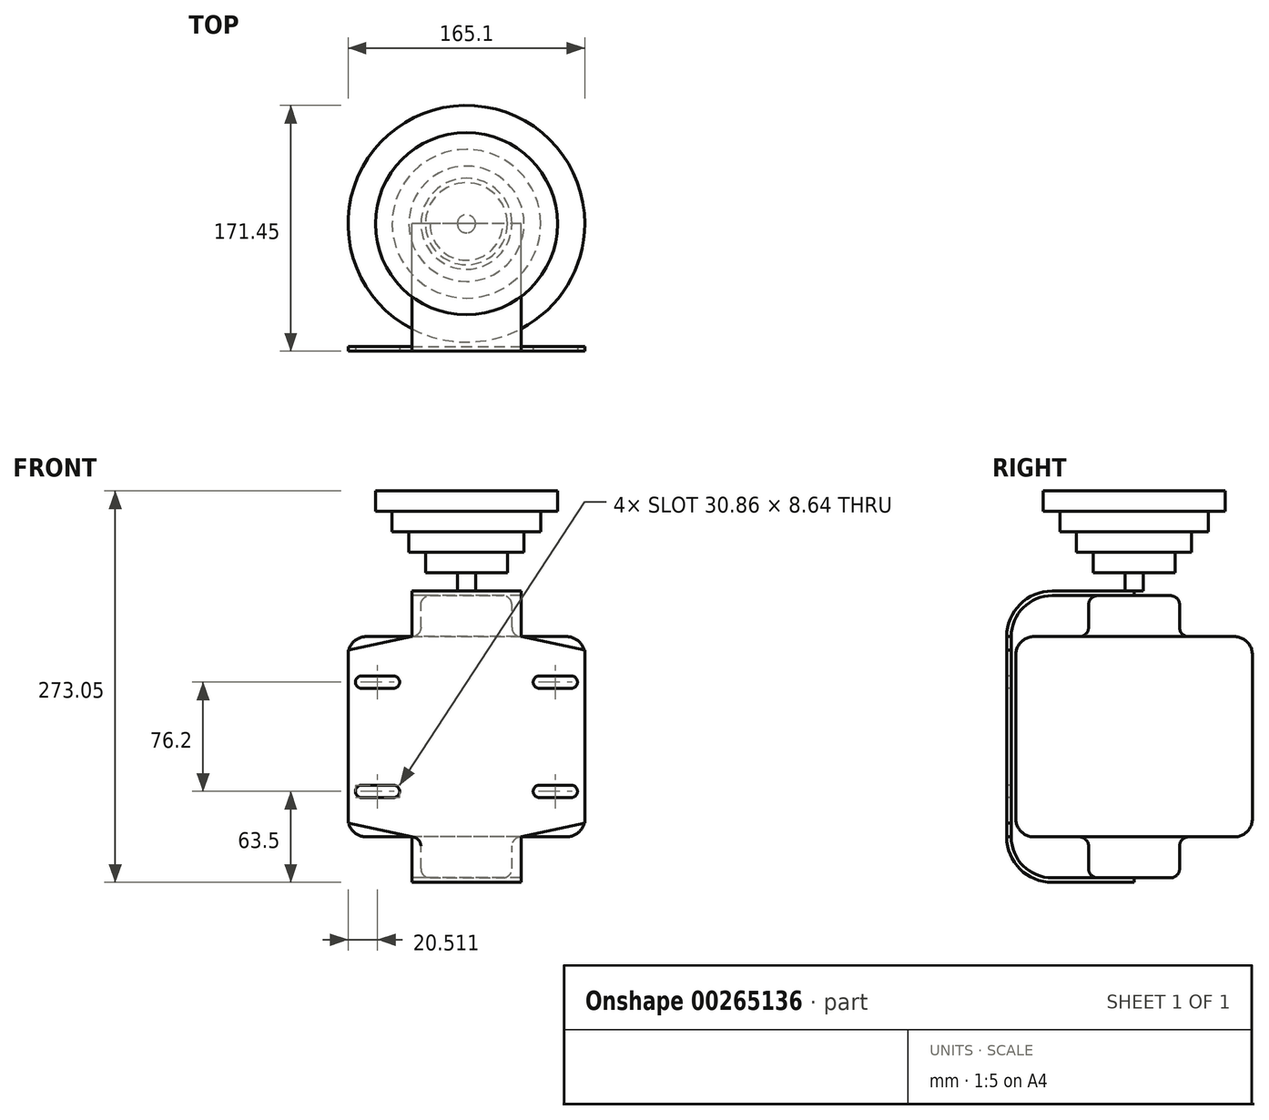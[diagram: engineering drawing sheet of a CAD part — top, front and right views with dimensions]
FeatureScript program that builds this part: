
annotation { "Feature Type Name" : "Feature", "Feature Type Description" : "" }
export const myFeature = defineFeature(function(context is Context, id is Id, definition is map)
    precondition{}
    {
        {
            var Q0;
            Q0=qCreatedBy(makeId("Front.planeOp"),FACE);
            var sketch = newSketch(context, id + "F0", { "sketchPlane" : qUnion([Q0])});
            skLineSegment(sketch, "E0.bottom", {"start": v(-82.55, 60.33) * mm, "end": v(82.55, 60.33) * mm, "construction": true});
            skLineSegment(sketch, "E0.top", {"start": v(-82.55, -60.33) * mm, "end": v(82.55, -60.33) * mm, "construction": true});
            skLineSegment(sketch, "E0.left", {"start": v(-82.55, 60.33) * mm, "end": v(-82.55, -60.32) * mm});
            skLineSegment(sketch, "E0.right", {"start": v(82.55, 60.33) * mm, "end": v(82.55, -60.33) * mm});
            skPoint(sketch, "E0.middle", {"position": v(0, 0) * mm});
            skLineSegment(sketch, "E1", {"start": v(-82.55, 60.33) * mm, "end": v(-38.1, 69.85) * mm});
            skLineSegment(sketch, "E2", {"start": v(-38.1, 69.85) * mm, "end": v(38.1, 69.85) * mm});
            skLineSegment(sketch, "E3", {"start": v(38.1, 69.85) * mm, "end": v(82.55, 60.33) * mm});
            skLineSegment(sketch, "E4", {"start": v(-82.55, -60.33) * mm, "end": v(-38.1, -69.85) * mm});
            skLineSegment(sketch, "E5", {"start": v(-38.1, -69.85) * mm, "end": v(38.1, -69.85) * mm});
            skLineSegment(sketch, "E6", {"start": v(38.1, -69.85) * mm, "end": v(82.55, -60.33) * mm});
            skLineSegment(sketch, "E7", {"start": v(-73.15, 42.42) * mm, "end": v(-50.93, 42.42) * mm});
            skLineSegment(sketch, "E8", {"start": v(-73.15, 33.78) * mm, "end": v(-50.93, 33.78) * mm});
            skArc(sketch, "E9", {"start": v(-73.15, 42.42) * mm, "mid": v(-77.47, 38.1) * mm, "end": v(-73.15, 33.78) * mm});
            skArc(sketch, "E10", {"start": v(-50.93, 42.42) * mm, "mid": v(-46.6, 38.1) * mm, "end": v(-50.93, 33.78) * mm});
            skLineSegment(sketch, "E11", {"start": v(0, 0) * mm, "end": v(-102.96, 0) * mm, "construction": true});
            skPoint(sketch, "E11.endSnap0", {"position": v(-82.55, 0) * mm});
            skLineSegment(sketch, "E12", {"start": v(0, 0) * mm, "end": v(0, 55.5) * mm, "construction": true});
            skArc(sketch, "E13.MirrorCS", {"start": v(50.93, 42.42) * mm, "mid": v(46.6, 38.1) * mm, "end": v(50.93, 33.78) * mm});
            skLineSegment(sketch, "E14.MirrorCS", {"start": v(73.15, 42.42) * mm, "end": v(50.93, 42.42) * mm});
            skArc(sketch, "E15.MirrorCS", {"start": v(73.15, 42.42) * mm, "mid": v(77.47, 38.1) * mm, "end": v(73.15, 33.78) * mm});
            skLineSegment(sketch, "E16.MirrorCS", {"start": v(73.15, 33.78) * mm, "end": v(50.93, 33.78) * mm});
            skArc(sketch, "E17.MirrorCS", {"start": v(73.15, -42.42) * mm, "mid": v(77.47, -38.1) * mm, "end": v(73.15, -33.78) * mm});
            skArc(sketch, "E18.MirrorCS", {"start": v(50.93, -42.42) * mm, "mid": v(46.6, -38.1) * mm, "end": v(50.93, -33.78) * mm});
            skLineSegment(sketch, "E19.MirrorCS", {"start": v(73.15, -42.42) * mm, "end": v(50.93, -42.42) * mm});
            skLineSegment(sketch, "E20.MirrorCS", {"start": v(73.15, -33.78) * mm, "end": v(50.93, -33.78) * mm});
            skArc(sketch, "E21.MirrorCS", {"start": v(-73.15, -42.42) * mm, "mid": v(-77.47, -38.1) * mm, "end": v(-73.15, -33.78) * mm});
            skArc(sketch, "E22.MirrorCS", {"start": v(-50.93, -42.42) * mm, "mid": v(-46.6, -38.1) * mm, "end": v(-50.93, -33.78) * mm});
            skLineSegment(sketch, "E23.MirrorCS", {"start": v(-73.15, -33.78) * mm, "end": v(-50.93, -33.78) * mm});
            skLineSegment(sketch, "E24.MirrorCS", {"start": v(-73.15, -42.42) * mm, "end": v(-50.93, -42.42) * mm});
            skSolve(sketch);
        }
        {
            var Q0;
            Q0 = qSketchRegion(id + "F0", true);
            extrude(context, id + "F1", {"entities" : qUnion([Q0]), "oppositeDirection" : true, "depth" : 3.17 * mm});
        }
        {
            var Q0;
            Q0=qCreatedBy(makeId("Right.planeOp"),FACE);
            var sketch = newSketch(context, id + "F2", { "sketchPlane" : qUnion([Q0])});
            skLineSegment(sketch, "E25.0", {"start": v(0, -60.33) * mm, "end": v(0, -69.85) * mm, "construction": true});
            skArc(sketch, "E26", {"start": v(0, -69.85) * mm, "mid": v(9.3, -92.3) * mm, "end": v(31.75, -101.6) * mm});
            skLineSegment(sketch, "E27", {"start": v(31.75, -101.6) * mm, "end": v(88.9, -101.6) * mm});
            skLineSegment(sketch, "E28.0", {"start": v(31.75, -98.43) * mm, "end": v(88.9, -98.43) * mm});
            skArc(sketch, "E28.1", {"start": v(3.17, -69.85) * mm, "mid": v(11.54, -90.06) * mm, "end": v(31.75, -98.43) * mm});
            skLineSegment(sketch, "E29", {"start": v(3.17, -69.85) * mm, "end": v(0, -69.85) * mm});
            skLineSegment(sketch, "E30", {"start": v(88.9, -101.6) * mm, "end": v(88.9, -98.43) * mm});
            skLineSegment(sketch, "E31", {"start": v(0, 0) * mm, "end": v(80.59, 0) * mm, "construction": true});
            skLineSegment(sketch, "E32.MirrorCS", {"start": v(88.9, 101.6) * mm, "end": v(88.9, 98.43) * mm});
            skLineSegment(sketch, "E33.MirrorCS", {"start": v(3.17, 69.85) * mm, "end": v(0, 69.85) * mm});
            skLineSegment(sketch, "E34.MirrorCS", {"start": v(0, 60.33) * mm, "end": v(0, 69.85) * mm, "construction": true});
            skArc(sketch, "E35.MirrorCS", {"start": v(3.17, 69.85) * mm, "mid": v(11.54, 90.06) * mm, "end": v(31.75, 98.43) * mm});
            skArc(sketch, "E36.MirrorCS", {"start": v(0, 69.85) * mm, "mid": v(9.3, 92.3) * mm, "end": v(31.75, 101.6) * mm});
            skLineSegment(sketch, "E37.MirrorCS", {"start": v(31.75, 98.43) * mm, "end": v(88.9, 98.43) * mm});
            skLineSegment(sketch, "E38.MirrorCS", {"start": v(31.75, 101.6) * mm, "end": v(88.9, 101.6) * mm});
            skSolve(sketch);
        }
        {
            var Q0;
            Q0=makeQuery(id+"F2.imprint","IMPRINT",FACE,{"disambiguationData":[TD([[makeQuery(id+"F2.imprint","IMPRINT",EDGE,{"derivedFrom":sQuery(id+"F2.wireOp",EDGE,"E26")}),1.0]])]});
            var Q1;
            Q1=makeQuery(id+"F2.imprint","IMPRINT",FACE,{"disambiguationData":[TD([[makeQuery(id+"F2.imprint","IMPRINT",EDGE,{"derivedFrom":sQuery(id+"F2.wireOp",EDGE,"E32.MirrorCS")}),-1.0]])]});
            extrude(context, id + "F3", {"entities" : qUnion([Q0, Q1]), "operationType" : NewBodyOperationType.ADD, "endBound" : BoundingType.SYMMETRIC, "depth" : 76.2 * mm});
        }
        {
            var Q0;
            Q0=qCreatedBy(makeId("Right.planeOp"),FACE);
            var sketch = newSketch(context, id + "F4", { "sketchPlane" : qUnion([Q0])});
            skLineSegment(sketch, "E39", {"start": v(88.9, 116.6) * mm, "end": v(88.9, -125.52) * mm, "construction": true});
            skLineSegment(sketch, "E40", {"start": v(88.9, 98.43) * mm, "end": v(114.3, 98.43) * mm});
            skLineSegment(sketch, "E41", {"start": v(120.65, 92.08) * mm, "end": v(120.65, 76.2) * mm});
            skLineSegment(sketch, "E42", {"start": v(127, 69.85) * mm, "end": v(158.75, 69.85) * mm});
            skLineSegment(sketch, "E43", {"start": v(171.45, 57.15) * mm, "end": v(171.45, -57.15) * mm});
            skLineSegment(sketch, "E44", {"start": v(158.75, -69.85) * mm, "end": v(127, -69.85) * mm});
            skLineSegment(sketch, "E45", {"start": v(120.65, -76.2) * mm, "end": v(120.65, -92.08) * mm});
            skLineSegment(sketch, "E46", {"start": v(114.3, -98.43) * mm, "end": v(88.9, -98.43) * mm});
            skLineSegment(sketch, "E47", {"start": v(88.9, -98.43) * mm, "end": v(88.9, 98.43) * mm});
            skPoint(sketch, "E48.visualSharp", {"position": v(120.65, 98.43) * mm});
            skArc(sketch, "E48.filletArc", {"start": v(120.65, 92.08) * mm, "mid": v(118.8, 96.57) * mm, "end": v(114.3, 98.43) * mm});
            skPoint(sketch, "E49.visualSharp", {"position": v(120.65, -98.43) * mm});
            skArc(sketch, "E49.filletArc", {"start": v(114.3, -98.43) * mm, "mid": v(118.8, -96.57) * mm, "end": v(120.65, -92.08) * mm});
            skPoint(sketch, "E50.visualSharp", {"position": v(120.65, -69.85) * mm});
            skArc(sketch, "E50.filletArc", {"start": v(127, -69.85) * mm, "mid": v(122.5, -71.7) * mm, "end": v(120.65, -76.2) * mm});
            skPoint(sketch, "E51.visualSharp", {"position": v(120.65, 69.85) * mm});
            skArc(sketch, "E51.filletArc", {"start": v(120.65, 76.2) * mm, "mid": v(122.5, 71.7) * mm, "end": v(127, 69.85) * mm});
            skPoint(sketch, "E52.visualSharp", {"position": v(171.45, 69.85) * mm});
            skArc(sketch, "E52.filletArc", {"start": v(171.45, 57.15) * mm, "mid": v(167.73, 66.13) * mm, "end": v(158.75, 69.85) * mm});
            skPoint(sketch, "E53.visualSharp", {"position": v(171.45, -69.85) * mm});
            skArc(sketch, "E53.filletArc", {"start": v(158.75, -69.85) * mm, "mid": v(167.73, -66.13) * mm, "end": v(171.45, -57.15) * mm});
            skSolve(sketch);
        }
        {
            var Q0;
            Q0 = qSketchRegion(id + "F4", true);
            var Q1;
            Q1=sQuery(id+"F4.wireOp",EDGE,"E39");
            revolve(context, id + "F5", {"operationType" : NewBodyOperationType.ADD, "entities" : qUnion([Q0]), "axis" : qUnion([Q1]), "revolveType" : RevolveType.FULL});
        }
        {
            var Q0;
            Q0=qCreatedBy(makeId("Right.planeOp"),FACE);
            var sketch = newSketch(context, id + "F6", { "sketchPlane" : qUnion([Q0])});
            skLineSegment(sketch, "E54", {"start": v(82.55, 114.3) * mm, "end": v(60.33, 114.3) * mm});
            skLineSegment(sketch, "E55", {"start": v(88.9, 171.45) * mm, "end": v(25.4, 171.45) * mm});
            skLineSegment(sketch, "E56", {"start": v(25.4, 157.16) * mm, "end": v(37.04, 157.16) * mm});
            skLineSegment(sketch, "E57", {"start": v(37.04, 142.88) * mm, "end": v(48.68, 142.88) * mm});
            skLineSegment(sketch, "E58", {"start": v(88.9, 101.6) * mm, "end": v(88.9, 179.13) * mm, "construction": true});
            skLineSegment(sketch, "E59", {"start": v(25.4, 157.16) * mm, "end": v(25.4, 171.45) * mm});
            skLineSegment(sketch, "E60", {"start": v(37.04, 157.16) * mm, "end": v(37.04, 142.88) * mm});
            skLineSegment(sketch, "E61", {"start": v(48.68, 142.88) * mm, "end": v(48.68, 128.59) * mm});
            skLineSegment(sketch, "E62", {"start": v(48.68, 128.59) * mm, "end": v(60.33, 128.59) * mm});
            skLineSegment(sketch, "E63", {"start": v(60.32, 128.59) * mm, "end": v(60.32, 114.3) * mm});
            skLineSegment(sketch, "E64", {"start": v(88.9, 171.45) * mm, "end": v(88.9, 101.6) * mm});
            skLineSegment(sketch, "E65", {"start": v(82.55, 101.6) * mm, "end": v(82.55, 114.3) * mm});
            skLineSegment(sketch, "E66", {"start": v(82.55, 101.6) * mm, "end": v(88.9, 101.6) * mm});
            skSolve(sketch);
        }
        {
            var Q0;
            Q0 = qSketchRegion(id + "F6", true);
            var Q1;
            Q1=sQuery(id+"F6.wireOp",EDGE,"E58");
            revolve(context, id + "F7", {"operationType" : NewBodyOperationType.ADD, "entities" : qUnion([Q0]), "axis" : qUnion([Q1]), "revolveType" : RevolveType.FULL});
        }
    });
